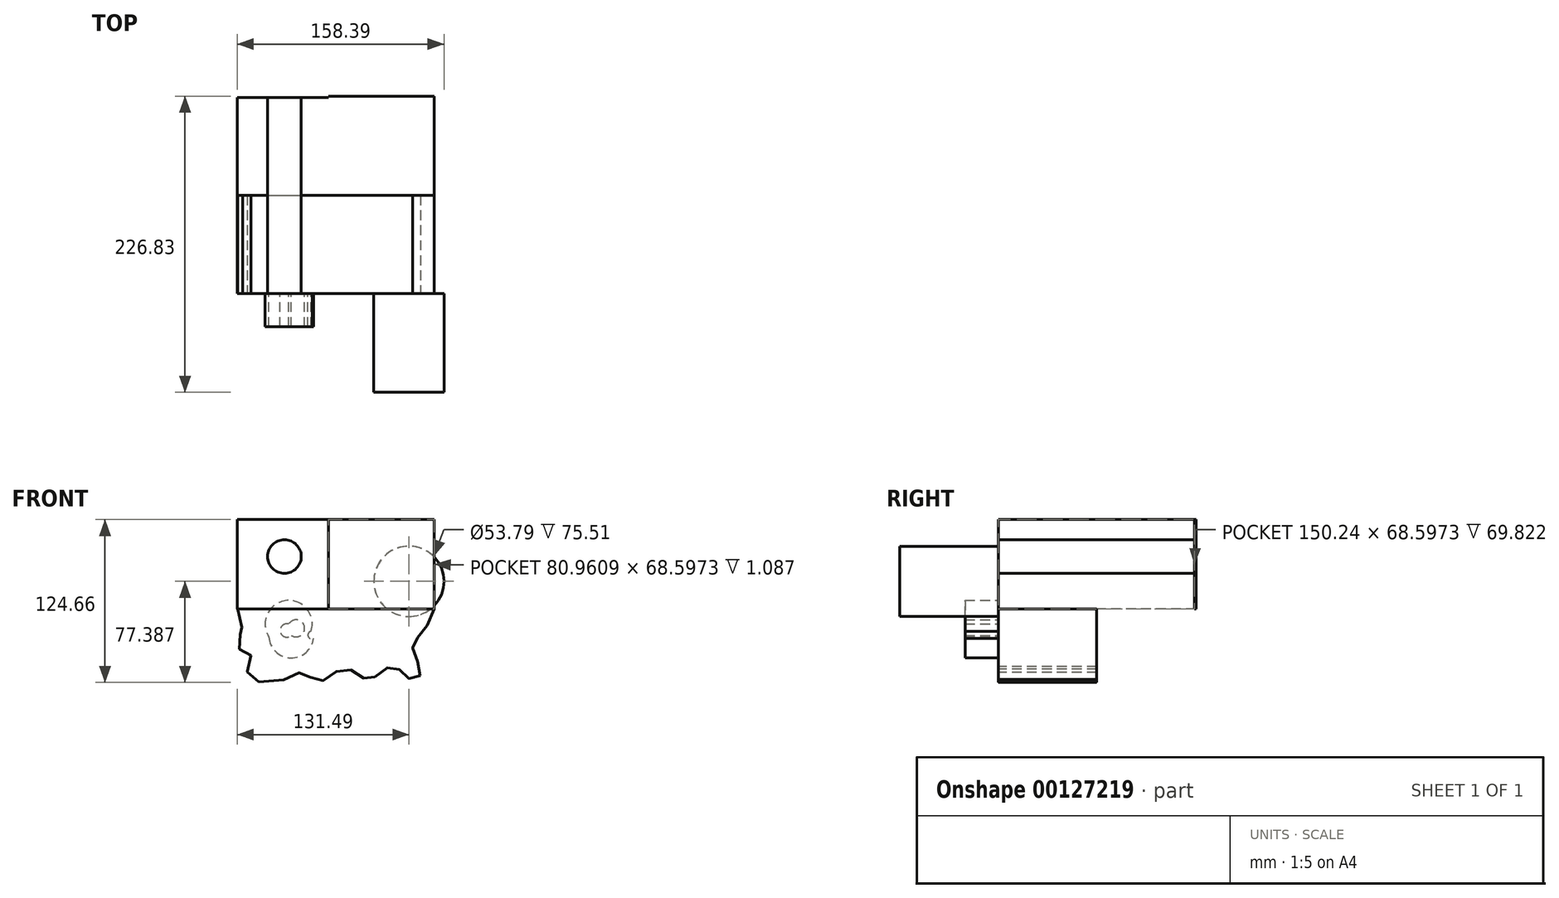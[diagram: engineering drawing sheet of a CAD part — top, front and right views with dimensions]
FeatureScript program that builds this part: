
annotation { "Feature Type Name" : "Feature", "Feature Type Description" : "" }
export const myFeature = defineFeature(function(context is Context, id is Id, definition is map)
    precondition{}
    {
        {
            var Q0;
            Q0=qCreatedBy(makeId("Top.planeOp"),FACE);
            var sketch = newSketch(context, id + "F0", { "sketchPlane" : qUnion([Q0])});
            skLineSegment(sketch, "E0.bottom", {"start": v(-74.98, 74.85) * mm, "end": v(-5.16, 74.85) * mm});
            skLineSegment(sketch, "E0.top", {"start": v(-74.98, -75.4) * mm, "end": v(-5.16, -75.4) * mm});
            skLineSegment(sketch, "E0.left", {"start": v(-74.98, 74.85) * mm, "end": v(-74.98, -75.4) * mm});
            skLineSegment(sketch, "E0.right", {"start": v(-5.16, 74.85) * mm, "end": v(-5.16, -75.4) * mm});
            skLineSegment(sketch, "E1.bottom", {"start": v(75.8, 75.93) * mm, "end": v(-5.16, 75.93) * mm});
            skLineSegment(sketch, "E1.top", {"start": v(75.8, -75.4) * mm, "end": v(-5.16, -75.4) * mm});
            skLineSegment(sketch, "E1.left", {"start": v(75.8, 75.93) * mm, "end": v(75.8, -75.4) * mm});
            skLineSegment(sketch, "E1.right", {"start": v(-5.16, 75.93) * mm, "end": v(-5.16, -75.4) * mm});
            skSolve(sketch);
        }
        {
            var Q0;
            Q0 = qSketchRegion(id + "F0", true);
            extrude(context, id + "F1", {"entities" : qUnion([Q0]), "depth" : 68.6 * mm});
        }
        {
            var Q0;
            Q0=makeQuery(id+"F1.opExtrude","SWEPT_FACE",FACE,{"disambiguationData":[OSD([sQuery(id+"F0.wireOp",EDGE,"E0.top"),sQuery(id+"F0.wireOp",EDGE,"E1.top")])]});
            var sketch = newSketch(context, id + "F2", { "sketchPlane" : qUnion([Q0])});
            skCircle(sketch, "E2", {"center": v(-38.85, 40.34) * mm, "radius": 12.88 * mm});
            skSolve(sketch);
        }
        {
            var Q0;
            Q0 = qSketchRegion(id + "F2", true);
            var Q1;
            Q1=makeQuery(id+"F1.opExtrude","SWEPT_FACE",FACE,{"disambiguationData":[OSD([sQuery(id+"F0.wireOp",EDGE,"E1.bottom")])]});
            extrude(context, id + "F3", {"entities" : qUnion([Q0]), "operationType" : NewBodyOperationType.REMOVE, "endBound" : BoundingType.UP_TO_SURFACE, "oppositeDirection" : true, "endBoundEntityFace" : qUnion([Q1]), "depth" : 39.62 * mm});
        }
        {
            var Q0;
            Q0=makeQuery(id+"F1.opExtrude","SWEPT_FACE",FACE,{"disambiguationData":[OSD([sQuery(id+"F0.wireOp",EDGE,"E0.top"),sQuery(id+"F0.wireOp",EDGE,"E1.top")])]});
            var sketch = newSketch(context, id + "F4", { "sketchPlane" : qUnion([Q0])});
            skCircle(sketch, "E3", {"center": v(56.5, 21.33) * mm, "radius": 26.9 * mm});
            skSolve(sketch);
        }
        {
            var Q0;
            Q0 = qSketchRegion(id + "F4", true);
            extrude(context, id + "F5", {"entities" : qUnion([Q0]), "operationType" : NewBodyOperationType.ADD, "depth" : 75.5 * mm});
        }
        {
            var Q0;
            Q0=qCreatedBy(makeId("Front.planeOp"),FACE);
            var sketch = newSketch(context, id + "F6", { "sketchPlane" : qUnion([Q0])});
            skFitSpline(sketch, "E4", {"points": [v(-74.64, 0) * mm, v(-70.84, -15.62) * mm, v(-70.84, -15.9) * mm, v(-74.64, -28.93) * mm, v(-64.86, -34.64) * mm, v(-66.76, -51.48) * mm, v(-37.15, -53.39) * mm, v(-24.65, -48.5) * mm, v(-12.7, -55.56) * mm, v(0, -48.22) * mm, v(14.2, -47.4) * mm, v(25.6, -54.2) * mm, v(36.2, -46.86) * mm, v(47.34, -44.96) * mm, v(55.77, -52.84) * mm, v(64.73, -51.48) * mm, v(62.29, -37.9) * mm, v(59.57, -26.76) * mm, v(67.18, -17.52) * mm, v(75.87, 0) * mm], "startDerivative": vector(88.1, -375.5) * mm, "endDerivative": vector(114.09, 298.05) * mm});
            skLineSegment(sketch, "E5", {"start": v(-74.64, 0) * mm, "end": v(75.87, 0) * mm});
            skSolve(sketch);
        }
        {
            var Q0;
            Q0 = qSketchRegion(id + "F6", true);
            var Q1;
            {var subQ0=sQuery(id+"F0.wireOp",EDGE,"E1.top");var subQ1=sQuery(id+"F0.wireOp",EDGE,"E0.top");var subQ2=sQuery(id+"F4.wireOp",EDGE,"E3");Q1=makeQuery(id+"F5.boolean.opBoolean","SPLIT",FACE,{"disambiguationData":[TD([makeQuery(id+"F1.opExtrude","CAP_FACE",FACE,{"disambiguationData":[OSD([sQuery(id+"F0.wireOp",EDGE,"E0.bottom"),subQ1,sQuery(id+"F0.wireOp",EDGE,"E0.left"),sQuery(id+"F0.wireOp",EDGE,"E1.bottom"),subQ0,sQuery(id+"F0.wireOp",EDGE,"E1.left"),sQuery(id+"F0.wireOp",EDGE,"E1.right")])],"isStart":true})])],"derivedFrom":makeQuery(id+"F5.opExtrude","CAP_FACE",FACE,{"disambiguationData":[OSD([subQ2])],"isStart":true})});}
            extrude(context, id + "F7", {"entities" : qUnion([Q0]), "operationType" : NewBodyOperationType.ADD, "endBound" : BoundingType.UP_TO_SURFACE, "endBoundEntityFace" : qUnion([Q1]), "depth" : 57.34 * mm});
        }
        {
            var Q0;
            {var subQ0=sQuery(id+"F0.wireOp",EDGE,"E1.left");var subQ1=makeQuery(id+"F1.opExtrude","SWEPT_FACE",FACE,{"disambiguationData":[OSD([subQ0])]});var subQ2=sQuery(id+"F4.wireOp",EDGE,"E3");var subQ3=makeQuery(id+"F5.opExtrude","SWEPT_FACE",FACE,{"disambiguationData":[OSD([subQ2])]});var subQ4=sQuery(id+"F0.wireOp",EDGE,"E0.left");var subQ5=sQuery(id+"F0.wireOp",EDGE,"E1.right");var subQ6=sQuery(id+"F0.wireOp",EDGE,"E1.top");var subQ7=sQuery(id+"F0.wireOp",EDGE,"E1.bottom");var subQ8=sQuery(id+"F0.wireOp",EDGE,"E0.top");var subQ9=sQuery(id+"F0.wireOp",EDGE,"E0.bottom");var subQ10=makeQuery(id+"F1.opExtrude","CAP_FACE",FACE,{"disambiguationData":[OSD([subQ9,subQ8,subQ4,subQ7,subQ6,subQ0,subQ5])],"isStart":true});var subQ11=makeQuery(id+"F5.opExtrude","CAP_FACE",FACE,{"disambiguationData":[OSD([subQ2])],"isStart":true});var subQ12=makeQuery(id+"F1.opExtrude","SWEPT_FACE",FACE,{"disambiguationData":[OSD([subQ8,subQ6])]});Q0=makeQuery(id+"F7.boolean.opBoolean","MERGE",FACE,{"derivedFrom":[makeQuery(id+"F5.boolean.opBoolean","SPLIT",FACE,{"disambiguationData":[TD([subQ10,subQ1,subQ3,subQ11])],"derivedFrom":subQ12}),makeQuery(id+"F5.boolean.opBoolean","SPLIT",FACE,{"disambiguationData":[TD([subQ10,makeQuery(id+"F1.opExtrude","CAP_FACE",FACE,{"disambiguationData":[OSD([subQ9,subQ8,subQ4,subQ7,subQ6,subQ0,subQ5])],"isStart":false}),makeQuery(id+"F1.opExtrude","SWEPT_FACE",FACE,{"disambiguationData":[OSD([subQ4])]}),subQ1,makeQuery(id+"F3.boolean.opBoolean","COPY",FACE,{"derivedFrom":makeQuery(id+"F3.opExtrude","SWEPT_FACE",FACE,{"disambiguationData":[OSD([sQuery(id+"F2.wireOp",EDGE,"E2")])]})}),subQ3,subQ11])],"derivedFrom":subQ12}),makeQuery(id+"F7.opExtrude","CAP_FACE",FACE,{"disambiguationData":[OSD([sQuery(id+"F6.wireOp",EDGE,"E4"),sQuery(id+"F6.wireOp",EDGE,"E5")])],"isStart":false})]});}
            var sketch = newSketch(context, id + "F8", { "sketchPlane" : qUnion([Q0])});
            skArc(sketch, "E6", {"start": v(-50.73, -21.33) * mm, "mid": v(-34.1, -37.38) * mm, "end": v(-16.5, -22.41) * mm});
            skArc(sketch, "E7", {"start": v(-18.4, -16.98) * mm, "mid": v(-38.02, 6.5) * mm, "end": v(-50.73, -21.33) * mm});
            skArc(sketch, "E8", {"start": v(-35.6, -11.42) * mm, "mid": v(-42, -17.53) * mm, "end": v(-33.56, -20.18) * mm});
            skArc(sketch, "E9", {"start": v(-33.56, -20.18) * mm, "mid": v(-23.55, -13.23) * mm, "end": v(-35.6, -11.42) * mm});
            skArc(sketch, "E10", {"start": v(-18.4, -16.98) * mm, "mid": v(-20.7, -20.84) * mm, "end": v(-16.5, -22.41) * mm});
            skSolve(sketch);
        }
        {
            var Q0;
            Q0 = qSketchRegion(id + "F8", true);
            extrude(context, id + "F9", {"entities" : qUnion([Q0]), "operationType" : NewBodyOperationType.ADD, "depth" : 25.4 * mm});
        }
    });
